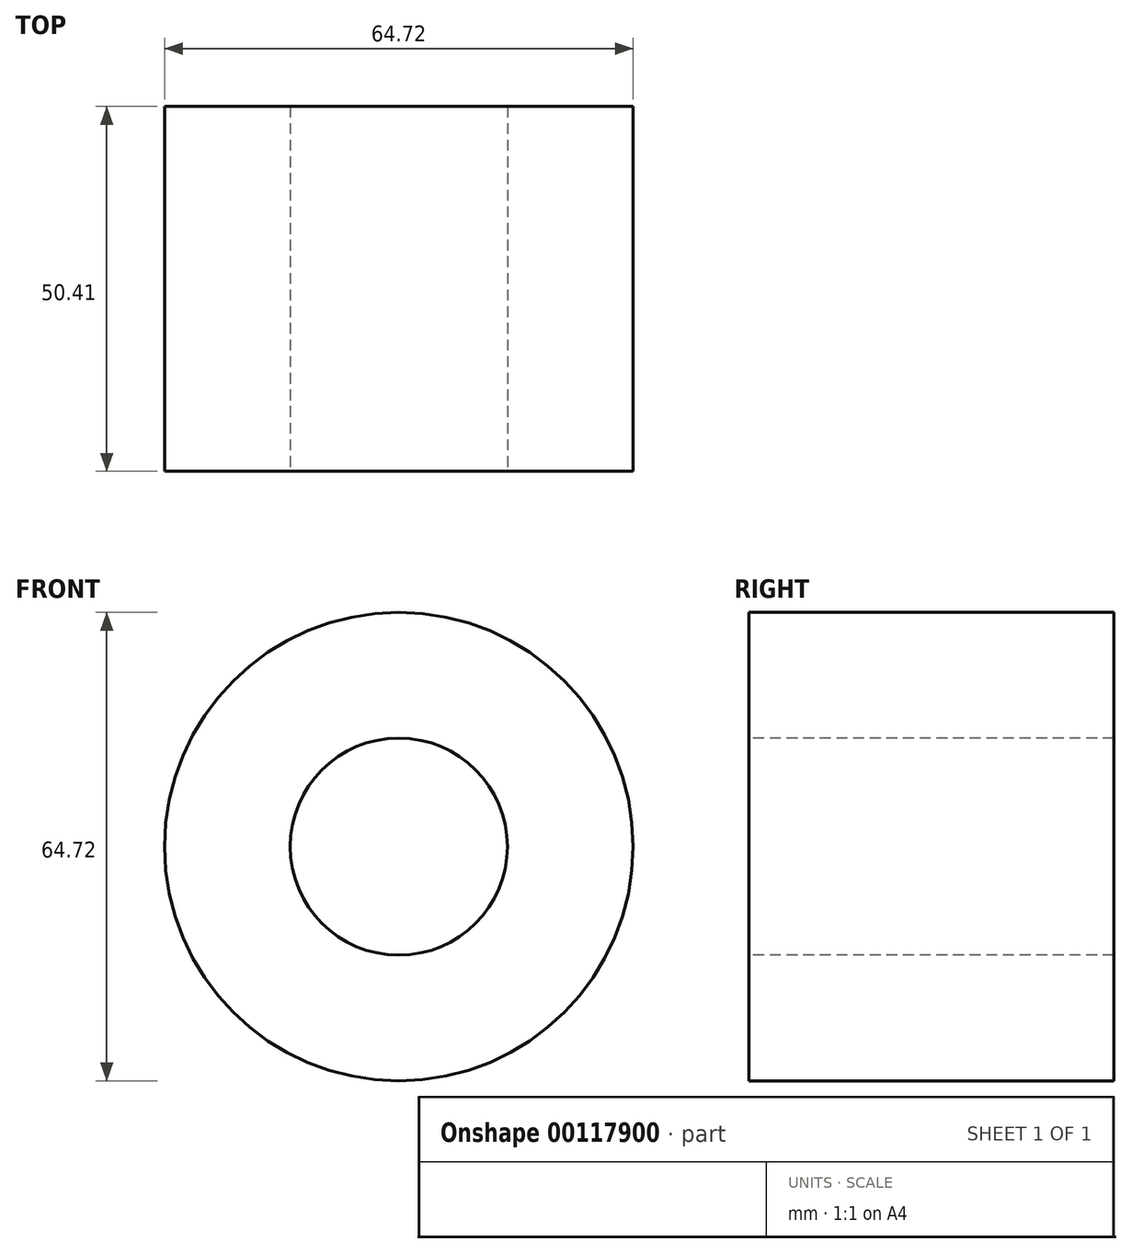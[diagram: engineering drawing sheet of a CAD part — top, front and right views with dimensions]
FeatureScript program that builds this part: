
annotation { "Feature Type Name" : "Feature", "Feature Type Description" : "" }
export const myFeature = defineFeature(function(context is Context, id is Id, definition is map)
    precondition{}
    {
        {
            var Q0;
            Q0=qCreatedBy(makeId("Front.planeOp"),FACE);
            var sketch = newSketch(context, id + "F0", { "sketchPlane" : qUnion([Q0])});
            skCircle(sketch, "E0", {"center": v(0, 0) * mm, "radius": 32.36 * mm});
            skSolve(sketch);
        }
        {
            var Q0;
            Q0=makeQuery(id+"F0.imprint","IMPRINT",FACE,{"disambiguationData":[TD([[makeQuery(id+"F0.imprint","IMPRINT",EDGE,{"derivedFrom":sQuery(id+"F0.wireOp",EDGE,"E0")}),1.0]])]});
            var Q1;
            Q1=sQuery(id+"F0.wireOp",EDGE,"E0");
            extrude(context, id + "F1", {"entities" : qUnion([Q0]), "surfaceEntities" : qUnion([Q1]), "depth" : 50.4 * mm});
        }
        {
            var Q0;
            Q0=makeQuery(id+"F1.opExtrude","CAP_FACE",FACE,{"disambiguationData":[OSD([sQuery(id+"F0.wireOp",EDGE,"E0")])],"isStart":false});
            var sketch = newSketch(context, id + "F2", { "sketchPlane" : qUnion([Q0])});
            skCircle(sketch, "E1", {"center": v(0, 0) * mm, "radius": 15 * mm});
            skSolve(sketch);
        }
        {
            var Q0;
            Q0=makeQuery(id+"F2.imprint","IMPRINT",FACE,{"disambiguationData":[TD([[makeQuery(id+"F2.imprint","IMPRINT",EDGE,{"derivedFrom":sQuery(id+"F2.wireOp",EDGE,"E1")}),1.0]])]});
            extrude(context, id + "F3", {"entities" : qUnion([Q0]), "operationType" : NewBodyOperationType.REMOVE, "endBound" : BoundingType.THROUGH_ALL, "oppositeDirection" : true, "depth" : 25.4 * mm});
        }
    });
